# Revit family: Wentylatory promieniowe FRv 125-280
name_source: partatom
category: Mechanical Equipment
revit_build: Autodesk Revit 2015 (Build: 20140606_1530(x64)
units: mm (PartAtom-declared; Revit-internal decimal feet)

## types (46) — shared parameters
Manufacturer = Chemowent
URL = http://chemowent.pl

## per-type parameters (varying)
| type | Ciśnienie maksymalne | Ilość biegunów | Moc nominalna | Natężenie znamionowe przy 400V/50Hz | Prędkość obrotowa przy 50Hz | Waga | Wydajność maksymalna | Zakres prędkości obrotowej (10Hz) | Zakres prędkości obrotowej (60Hz) | podstawa - długość | podstawa - szerokość | promień | stelaż - pozycja | stelaż - wysokość | typ wentylatora | średnica nominalna |
| FRv 125 (1500) | 130.0 Pa | 4 | 0.060 kW | 0.350 A | 1500 | 11.00 kg | 375.0 m³/h | 266 | 1596 | 250 mm  [stored 0.82021 ft] | 250 mm  [stored 0.82021 ft] | 63 mm | 73 mm | 285 mm  [stored 0.935039 ft] | FRv 125-280 : FRv 125 / FRv 125/140 | 125 mm  [stored 0.410105 ft] |
| FRv 125 (3000) | 530.0 Pa | 2 | 0.120 kW | 0.500 A | 3000 | 11.00 kg | 735.0 m³/h | 544 | 3264 | 250 mm  [stored 0.82021 ft] | 250 mm  [stored 0.82021 ft] | 63 mm | 73 mm | 285 mm  [stored 0.935039 ft] | FRv 125-280 : FRv 125 / FRv 125/140 | 125 mm  [stored 0.410105 ft] |
| FRv 125 EX (1500) | 130.0 Pa | 4 | 0.120 kW | 0.480 A | 1500 | 15.00 kg | 375.0 m³/h | 0 | 0 | 250 mm  [stored 0.82021 ft] | 250 mm  [stored 0.82021 ft] | 63 mm | 73 mm | 285 mm  [stored 0.935039 ft] | FRv 125-280 : FRv 125 / FRv 125/140 | 125 mm  [stored 0.410105 ft] |
| FRv 125 EX (3000) | 530.0 Pa | 2 | 0.180 kW | 0.530 A | 3000 | 15.00 kg | 735.0 m³/h | 0 | 0 | 250 mm  [stored 0.82021 ft] | 250 mm  [stored 0.82021 ft] | 63 mm | 73 mm | 285 mm  [stored 0.935039 ft] | FRv 125-280 : FRv 125 / FRv 125/140 | 125 mm  [stored 0.410105 ft] |
| FRv 125/140 (1500) | 140.0 Pa | 4 | 0.060 kW | 0.350 A | 1500 | 11.00 kg | 380.0 m³/h | 266 | 1596 | 250 mm  [stored 0.82021 ft] | 250 mm  [stored 0.82021 ft] | 63 mm | 73 mm | 285 mm  [stored 0.935039 ft] | FRv 125-280 : FRv 125 / FRv 125/140 | 125 mm  [stored 0.410105 ft] |
| FRv 125/140 (3000) | 560.0 Pa | 2 | 0.120 kW | 0.500 A | 3000 | 11.00 kg | 790.0 m³/h | 544 | 3264 | 250 mm  [stored 0.82021 ft] | 250 mm  [stored 0.82021 ft] | 63 mm | 73 mm | 285 mm  [stored 0.935039 ft] | FRv 125-280 : FRv 125 / FRv 125/140 | 125 mm  [stored 0.410105 ft] |
| FRv 125/140 EX (1500) | 140.0 Pa | 4 | 0.120 kW | 0.480 A | 1500 | 15.00 kg | 380.0 m³/h | 0 | 0 | 250 mm  [stored 0.82021 ft] | 250 mm  [stored 0.82021 ft] | 63 mm | 73 mm | 285 mm  [stored 0.935039 ft] | FRv 125-280 : FRv 125 / FRv 125/140 | 125 mm  [stored 0.410105 ft] |
| FRv 125/140 EX (3000) | 560.0 Pa | 2 | 0.180 kW | 0.530 A | 3000 | 15.00 kg | 790.0 m³/h | 0 | 0 | 250 mm  [stored 0.82021 ft] | 250 mm  [stored 0.82021 ft] | 63 mm | 73 mm | 285 mm  [stored 0.935039 ft] | FRv 125-280 : FRv 125 / FRv 125/140 | 125 mm  [stored 0.410105 ft] |
| FRv 160 (3000) | 820.0 Pa | 2 | 0.370 kW | 1.100 A | 3000 | 15.00 kg | 1220.0 m³/h | 544 | 3264 | 300 mm | 300 mm | 80 mm  [stored 0.262467 ft] | 90 mm  [stored 0.295276 ft] | 440 mm  [stored 1.44357 ft] | FRv 125-280 : FRv 160 / FRv 160/180 | 160 mm  [stored 0.524934 ft] |
| FRv 160 (1500) | 200.0 Pa | 4 | 0.120 kW | 0.700 A | 1500 | 15.00 kg | 590.0 m³/h | 266 | 1596 | 300 mm | 300 mm | 80 mm  [stored 0.262467 ft] | 90 mm  [stored 0.295276 ft] | 440 mm  [stored 1.44357 ft] | FRv 125-280 : FRv 160 / FRv 160/180 | 160 mm  [stored 0.524934 ft] |
| FRv 160 (1000) | 0.0 Pa | 6 | 0.120 kW | 0.630 A | 1000 | 15.00 kg | 0.0 m³/h | 178 | 1068 | 300 mm | 300 mm | 80 mm  [stored 0.262467 ft] | 90 mm  [stored 0.295276 ft] | 440 mm  [stored 1.44357 ft] | FRv 125-280 : FRv 160 / FRv 160/180 | 160 mm  [stored 0.524934 ft] |
| FRv 160 (750) | 0.0 Pa | 8 | 0.120 kW | 0.800 A | 750 | 15.00 kg | 0.0 m³/h | 130 | 780 | 300 mm | 300 mm | 80 mm  [stored 0.262467 ft] | 90 mm  [stored 0.295276 ft] | 440 mm  [stored 1.44357 ft] | FRv 125-280 : FRv 160 / FRv 160/180 | 160 mm  [stored 0.524934 ft] |
| FRv 160 EX (3000) | 820.0 Pa | 2 | 0.370 kW | 0.970 A | 3000 | 20.00 kg | 1220.0 m³/h | 0 | 0 | 300 mm | 300 mm | 80 mm  [stored 0.262467 ft] | 90 mm  [stored 0.295276 ft] | 440 mm  [stored 1.44357 ft] | FRv 125-280 : FRv 160 / FRv 160/180 | 160 mm  [stored 0.524934 ft] |
| FRv 160 EX (1500) | 200.0 Pa | 4 | 0.120 kW | 0.480 A | 1500 | 20.00 kg | 590.0 m³/h | 0 | 0 | 300 mm | 300 mm | 80 mm  [stored 0.262467 ft] | 90 mm  [stored 0.295276 ft] | 440 mm  [stored 1.44357 ft] | FRv 125-280 : FRv 160 / FRv 160/180 | 160 mm  [stored 0.524934 ft] |
| FRv 160/180 (3000) | 990.0 Pa | 2 | 0.370 kW | 1.100 A | 3000 | 15.00 kg | 1700.0 m³/h | 544 | 3264 | 300 mm | 300 mm | 80 mm  [stored 0.262467 ft] | 90 mm  [stored 0.295276 ft] | 440 mm  [stored 1.44357 ft] | FRv 125-280 : FRv 160 / FRv 160/180 | 160 mm  [stored 0.524934 ft] |
| FRv 160/180 (1500) | 240.0 Pa | 4 | 0.120 kW | 0.700 A | 1500 | 15.00 kg | 860.0 m³/h | 266 | 1596 | 300 mm | 300 mm | 80 mm  [stored 0.262467 ft] | 90 mm  [stored 0.295276 ft] | 440 mm  [stored 1.44357 ft] | FRv 125-280 : FRv 160 / FRv 160/180 | 160 mm  [stored 0.524934 ft] |
| FRv 160/180 (1000) | 0.0 Pa | 6 | 0.120 kW | 0.630 A | 1000 | 15.00 kg | 0.0 m³/h | 178 | 1068 | 300 mm | 300 mm | 80 mm  [stored 0.262467 ft] | 90 mm  [stored 0.295276 ft] | 440 mm  [stored 1.44357 ft] | FRv 125-280 : FRv 160 / FRv 160/180 | 160 mm  [stored 0.524934 ft] |
| FRv 160/180 (750) | 0.0 Pa | 8 | 0.120 kW | 0.800 A | 750 | 15.00 kg | 0.0 m³/h | 130 | 780 | 300 mm | 300 mm | 80 mm  [stored 0.262467 ft] | 90 mm  [stored 0.295276 ft] | 440 mm  [stored 1.44357 ft] | FRv 125-280 : FRv 160 / FRv 160/180 | 160 mm  [stored 0.524934 ft] |
| FRv 160/180 EX (3000) | 990.0 Pa | 2 | 0.370 kW | 0.970 A | 3000 | 20.00 kg | 1700.0 m³/h | 0 | 0 | 300 mm | 300 mm | 80 mm  [stored 0.262467 ft] | 90 mm  [stored 0.295276 ft] | 440 mm  [stored 1.44357 ft] | FRv 125-280 : FRv 160 / FRv 160/180 | 160 mm  [stored 0.524934 ft] |
| FRv 160/180 EX (1500) | 240.0 Pa | 4 | 0.120 kW | 0.480 A | 1500 | 20.00 kg | 860.0 m³/h | 0 | 0 | 300 mm | 300 mm | 80 mm  [stored 0.262467 ft] | 90 mm  [stored 0.295276 ft] | 440 mm  [stored 1.44357 ft] | FRv 125-280 : FRv 160 / FRv 160/180 | 160 mm  [stored 0.524934 ft] |
| FRv 200 (3000) | 1420.0 Pa | 2 | 0.750 kW | 2.000 A | 3000 | 25.00 kg | 2800.0 m³/h | 564 | 3384 | 400 mm  [stored 1.31234 ft] | 400 mm  [stored 1.31234 ft] | 100 mm  [stored 0.328084 ft] | 110 mm  [stored 0.360892 ft] | 550 mm | FRv 125-280 : FRv 200 / FRv 200/225 | 200 mm  [stored 0.656168 ft] |
| FRv 200 (1500) | 310.0 Pa | 4 | 0.250 kW | 0.860 A | 1500 | 25.00 kg | 1300.0 m³/h | 266 | 1596 | 400 mm  [stored 1.31234 ft] | 400 mm  [stored 1.31234 ft] | 100 mm  [stored 0.328084 ft] | 110 mm  [stored 0.360892 ft] | 550 mm | FRv 125-280 : FRv 200 / FRv 200/225 | 200 mm  [stored 0.656168 ft] |
| FRv 200 (1000) | 0.0 Pa | 6 | 0.180 kW | 1.000 A | 1000 | 25.00 kg | 0.0 m³/h | 178 | 1068 | 400 mm  [stored 1.31234 ft] | 400 mm  [stored 1.31234 ft] | 100 mm  [stored 0.328084 ft] | 110 mm  [stored 0.360892 ft] | 550 mm | FRv 125-280 : FRv 200 / FRv 200/225 | 200 mm  [stored 0.656168 ft] |
| FRv 200 (750) | 0.0 Pa | 8 | 0.120 kW | 0.800 A | 750 | 25.00 kg | 0.0 m³/h | 130 | 780 | 400 mm  [stored 1.31234 ft] | 400 mm  [stored 1.31234 ft] | 100 mm  [stored 0.328084 ft] | 110 mm  [stored 0.360892 ft] | 550 mm | FRv 125-280 : FRv 200 / FRv 200/225 | 200 mm  [stored 0.656168 ft] |
| FRv 200 EX (3000) | 1420.0 Pa | 2 | 0.750 kW | 1.760 A | 3000 | 30.00 kg | 2800.0 m³/h | 0 | 0 | 400 mm  [stored 1.31234 ft] | 400 mm  [stored 1.31234 ft] | 100 mm  [stored 0.328084 ft] | 110 mm  [stored 0.360892 ft] | 550 mm | FRv 125-280 : FRv 200 / FRv 200/225 | 200 mm  [stored 0.656168 ft] |
| FRv 200 EX (1500) | 310.0 Pa | 4 | 0.250 kW | 0.790 A | 1500 | 30.00 kg | 1300.0 m³/h | 0 | 0 | 400 mm  [stored 1.31234 ft] | 400 mm  [stored 1.31234 ft] | 100 mm  [stored 0.328084 ft] | 110 mm  [stored 0.360892 ft] | 550 mm | FRv 125-280 : FRv 200 / FRv 200/225 | 200 mm  [stored 0.656168 ft] |
| FRv 200/225 (3000) | 1760.0 Pa | 2 | 1.100 kW | 2.600 A | 3000 | 25.00 kg | 3430.0 m³/h | 552 | 3312 | 400 mm  [stored 1.31234 ft] | 400 mm  [stored 1.31234 ft] | 100 mm  [stored 0.328084 ft] | 110 mm  [stored 0.360892 ft] | 550 mm | FRv 125-280 : FRv 200 / FRv 200/225 | 200 mm  [stored 0.656168 ft] |
| FRv 200/225 (1500) | 400.0 Pa | 4 | 0.250 kW | 0.860 A | 1500 | 25.00 kg | 1680.0 m³/h | 266 | 1596 | 400 mm  [stored 1.31234 ft] | 400 mm  [stored 1.31234 ft] | 100 mm  [stored 0.328084 ft] | 110 mm  [stored 0.360892 ft] | 550 mm | FRv 125-280 : FRv 200 / FRv 200/225 | 200 mm  [stored 0.656168 ft] |
| FRv 200/225 (1000) | 0.0 Pa | 6 | 0.180 kW | 1.000 A | 1000 | 25.00 kg | 0.0 m³/h | 178 | 1068 | 400 mm  [stored 1.31234 ft] | 400 mm  [stored 1.31234 ft] | 100 mm  [stored 0.328084 ft] | 110 mm  [stored 0.360892 ft] | 550 mm | FRv 125-280 : FRv 200 / FRv 200/225 | 200 mm  [stored 0.656168 ft] |
| FRv 200/225 (750) | 0.0 Pa | 8 | 0.120 kW | 0.800 A | 750 | 25.00 kg | 0.0 m³/h | 130 | 780 | 400 mm  [stored 1.31234 ft] | 400 mm  [stored 1.31234 ft] | 100 mm  [stored 0.328084 ft] | 110 mm  [stored 0.360892 ft] | 550 mm | FRv 125-280 : FRv 200 / FRv 200/225 | 200 mm  [stored 0.656168 ft] |
| FRv 200/225 EX (3000) | 1760.0 Pa | 2 | 1.100 kW | 2.600 A | 3000 | 30.00 kg | 3430.0 m³/h | 0 | 0 | 400 mm  [stored 1.31234 ft] | 400 mm  [stored 1.31234 ft] | 100 mm  [stored 0.328084 ft] | 110 mm  [stored 0.360892 ft] | 550 mm | FRv 125-280 : FRv 200 / FRv 200/225 | 200 mm  [stored 0.656168 ft] |
| FRv 200/225 EX (1500) | 400.0 Pa | 4 | 0.250 kW | 0.790 A | 1500 | 30.00 kg | 1680.0 m³/h | 0 | 0 | 400 mm  [stored 1.31234 ft] | 400 mm  [stored 1.31234 ft] | 100 mm  [stored 0.328084 ft] | 110 mm  [stored 0.360892 ft] | 550 mm | FRv 125-280 : FRv 200 / FRv 200/225 | 200 mm  [stored 0.656168 ft] |
| FRv 200/225 EX (1000) | 0.0 Pa | 6 | 0.370 kW | 1.300 A | 1000 | 30.00 kg | 0.0 m³/h | 0 | 0 | 400 mm  [stored 1.31234 ft] | 400 mm  [stored 1.31234 ft] | 100 mm  [stored 0.328084 ft] | 110 mm  [stored 0.360892 ft] | 550 mm | FRv 125-280 : FRv 200 / FRv 200/225 | 200 mm  [stored 0.656168 ft] |
| FRv 200/225 EX (750) | 0.0 Pa | 8 | 0.120 kW | 0.780 A | 750 | 30.00 kg | 0.0 m³/h | 0 | 0 | 400 mm  [stored 1.31234 ft] | 400 mm  [stored 1.31234 ft] | 100 mm  [stored 0.328084 ft] | 110 mm  [stored 0.360892 ft] | 550 mm | FRv 125-280 : FRv 200 / FRv 200/225 | 200 mm  [stored 0.656168 ft] |
| FRv 250 (1500) | 500.0 Pa | 4 | 0.370 kW | 1.200 A | 1500 | 30.00 kg | 2500.0 m³/h | 268 | 1608 | 450 mm  [stored 1.47638 ft] | 450 mm  [stored 1.47638 ft] | 125 mm  [stored 0.410105 ft] | 135 mm  [stored 0.442913 ft] | 686 mm  [stored 2.25066 ft] | FRv 125-280 : FRv 250 / FRv 250/280 | 250 mm  [stored 0.82021 ft] |
| FRv 250 (1000) | 220.0 Pa | 6 | 0.180 kW | 1.000 A | 1000 | 30.00 kg | 1700.0 m³/h | 178 | 1068 | 450 mm  [stored 1.47638 ft] | 450 mm  [stored 1.47638 ft] | 125 mm  [stored 0.410105 ft] | 135 mm  [stored 0.442913 ft] | 686 mm  [stored 2.25066 ft] | FRv 125-280 : FRv 250 / FRv 250/280 | 250 mm  [stored 0.82021 ft] |
| FRv 250 (750) | 110.0 Pa | 8 | 0.120 kW | 0.800 A | 750 | 30.00 kg | 1200.0 m³/h | 130 | 780 | 450 mm  [stored 1.47638 ft] | 450 mm  [stored 1.47638 ft] | 125 mm  [stored 0.410105 ft] | 135 mm  [stored 0.442913 ft] | 686 mm  [stored 2.25066 ft] | FRv 125-280 : FRv 250 / FRv 250/280 | 250 mm  [stored 0.82021 ft] |
| FRv 250 EX (1500) | 500.0 Pa | 4 | 0.370 kW | 0.790 A | 1500 | 35.00 kg | 2500.0 m³/h | 0 | 0 | 450 mm  [stored 1.47638 ft] | 450 mm  [stored 1.47638 ft] | 125 mm  [stored 0.410105 ft] | 135 mm  [stored 0.442913 ft] | 686 mm  [stored 2.25066 ft] | FRv 125-280 : FRv 250 / FRv 250/280 | 250 mm  [stored 0.82021 ft] |
| FRv 250 EX (1000) | 220.0 Pa | 6 | 0.370 kW | 1.300 A | 1000 | 35.00 kg | 1700.0 m³/h | 0 | 0 | 450 mm  [stored 1.47638 ft] | 450 mm  [stored 1.47638 ft] | 125 mm  [stored 0.410105 ft] | 135 mm  [stored 0.442913 ft] | 686 mm  [stored 2.25066 ft] | FRv 125-280 : FRv 250 / FRv 250/280 | 250 mm  [stored 0.82021 ft] |
| FRv 250 EX (750) | 110.0 Pa | 8 | 0.180 kW | 0.780 A | 750 | 35.00 kg | 1200.0 m³/h | 0 | 0 | 450 mm  [stored 1.47638 ft] | 450 mm  [stored 1.47638 ft] | 125 mm  [stored 0.410105 ft] | 135 mm  [stored 0.442913 ft] | 686 mm  [stored 2.25066 ft] | FRv 125-280 : FRv 250 / FRv 250/280 | 250 mm  [stored 0.82021 ft] |
| FRv 250/280 (1500) | 590.0 Pa | 4 | 0.550 kW | 1.500 A | 1500 | 30.00 kg | 3100.0 m³/h | 270 | 1620 | 450 mm  [stored 1.47638 ft] | 450 mm  [stored 1.47638 ft] | 125 mm  [stored 0.410105 ft] | 135 mm  [stored 0.442913 ft] | 686 mm  [stored 2.25066 ft] | FRv 125-280 : FRv 250 / FRv 250/280 | 250 mm  [stored 0.82021 ft] |
| FRv 250/280 (1000) | 260.0 Pa | 6 | 0.180 kW | 1.000 A | 1000 | 30.00 kg | 2050.0 m³/h | 178 | 1068 | 450 mm  [stored 1.47638 ft] | 450 mm  [stored 1.47638 ft] | 125 mm  [stored 0.410105 ft] | 135 mm  [stored 0.442913 ft] | 686 mm  [stored 2.25066 ft] | FRv 125-280 : FRv 250 / FRv 250/280 | 250 mm  [stored 0.82021 ft] |
| FRv 250/280 (750) | 140.0 Pa | 8 | 0.120 kW | 0.800 A | 750 | 30.00 kg | 1480.0 m³/h | 130 | 780 | 450 mm  [stored 1.47638 ft] | 450 mm  [stored 1.47638 ft] | 125 mm  [stored 0.410105 ft] | 135 mm  [stored 0.442913 ft] | 686 mm  [stored 2.25066 ft] | FRv 125-280 : FRv 250 / FRv 250/280 | 250 mm  [stored 0.82021 ft] |
| FRv 250/280 EX (1500) | 590.0 Pa | 4 | 0.550 kW | 1.590 A | 1500 | 35.00 kg | 3100.0 m³/h | 0 | 0 | 450 mm  [stored 1.47638 ft] | 450 mm  [stored 1.47638 ft] | 125 mm  [stored 0.410105 ft] | 135 mm  [stored 0.442913 ft] | 686 mm  [stored 2.25066 ft] | FRv 125-280 : FRv 250 / FRv 250/280 | 250 mm  [stored 0.82021 ft] |
| FRv 250/280 EX (1000) | 260.0 Pa | 6 | 0.370 kW | 1.300 A | 1000 | 35.00 kg | 2050.0 m³/h | 0 | 0 | 450 mm  [stored 1.47638 ft] | 450 mm  [stored 1.47638 ft] | 125 mm  [stored 0.410105 ft] | 135 mm  [stored 0.442913 ft] | 686 mm  [stored 2.25066 ft] | FRv 125-280 : FRv 250 / FRv 250/280 | 250 mm  [stored 0.82021 ft] |
| FRv 250/280 EX (750) | 140.0 Pa | 8 | 0.180 kW | 0.780 A | 750 | 35.00 kg | 1480.0 m³/h | 0 | 0 | 450 mm  [stored 1.47638 ft] | 450 mm  [stored 1.47638 ft] | 125 mm  [stored 0.410105 ft] | 135 mm  [stored 0.442913 ft] | 686 mm  [stored 2.25066 ft] | FRv 125-280 : FRv 250 / FRv 250/280 | 250 mm  [stored 0.82021 ft] |

note: [stored X ft] marks values corroborated as IEEE doubles in the binary element streams (Revit-internal decimal feet)

## geometry (parser evidence)
native form markers: Blend x4, Sweep x4
no freeform markers — native parametric forms only
